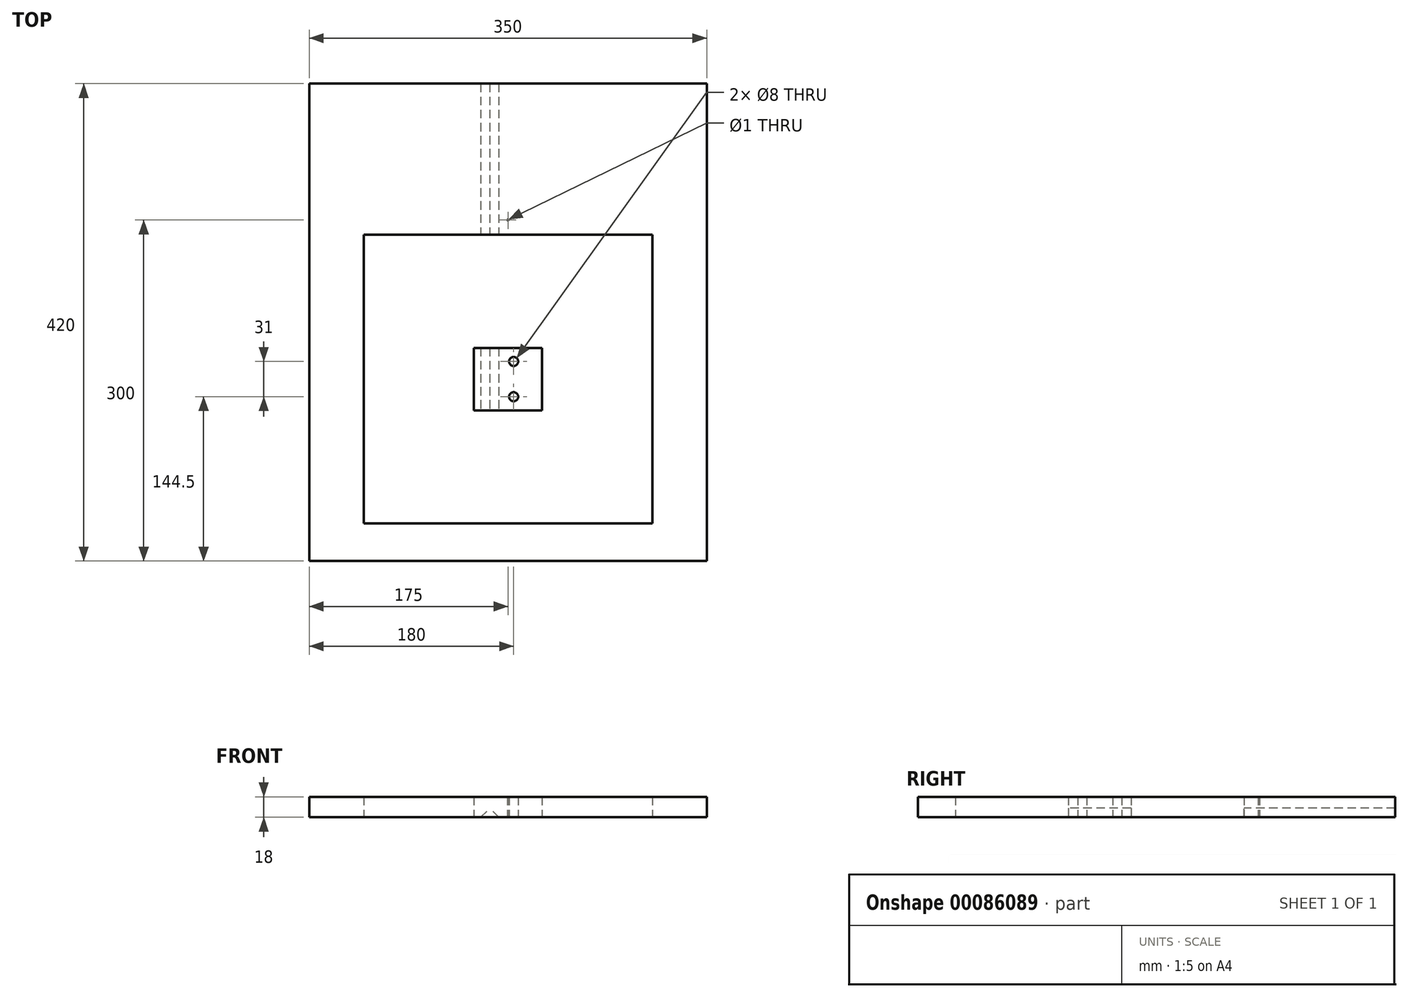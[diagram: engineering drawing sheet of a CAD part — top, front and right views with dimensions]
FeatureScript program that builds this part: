
annotation { "Feature Type Name" : "Feature", "Feature Type Description" : "" }
export const myFeature = defineFeature(function(context is Context, id is Id, definition is map)
    precondition{}
    {
        {
            var Q0;
            Q0=qCreatedBy(makeId("Top.planeOp"),FACE);
            var sketch = newSketch(context, id + "F0", { "sketchPlane" : qUnion([Q0])});
            skLineSegment(sketch, "E0.bottom", {"start": v(-175, 260) * mm, "end": v(175, 260) * mm});
            skLineSegment(sketch, "E0.top", {"start": v(-175, -160) * mm, "end": v(175, -160) * mm});
            skLineSegment(sketch, "E0.left", {"start": v(-175, 260) * mm, "end": v(-175, -160) * mm});
            skLineSegment(sketch, "E0.right", {"start": v(175, 260) * mm, "end": v(175, -160) * mm});
            skLineSegment(sketch, "E1.bottom", {"start": v(-107, 107) * mm, "end": v(107, 107) * mm, "construction": true});
            skLineSegment(sketch, "E1.top", {"start": v(-107, -107) * mm, "end": v(107, -107) * mm, "construction": true});
            skLineSegment(sketch, "E1.left", {"start": v(-107, 107) * mm, "end": v(-107, -107) * mm, "construction": true});
            skLineSegment(sketch, "E1.right", {"start": v(107, 107) * mm, "end": v(107, -107) * mm, "construction": true});
            skPoint(sketch, "E1.middle", {"position": v(0, 0) * mm});
            skLineSegment(sketch, "E2.bottom", {"start": v(-127, 127) * mm, "end": v(127, 127) * mm});
            skLineSegment(sketch, "E2.top", {"start": v(-127, -127) * mm, "end": v(127, -127) * mm});
            skLineSegment(sketch, "E2.left", {"start": v(-127, 127) * mm, "end": v(-127, -127) * mm});
            skLineSegment(sketch, "E2.right", {"start": v(127, 127) * mm, "end": v(127, -127) * mm});
            skPoint(sketch, "E3", {"position": v(0, 140) * mm});
            skPoint(sketch, "E3.positionSnap0", {"position": v(0, 260) * mm});
            skSolve(sketch);
        }
        {
            var Q0;
            Q0=makeQuery(id+"F0.imprint","IMPRINT",FACE,{"disambiguationData":[TD([[makeQuery(id+"F0.imprint","IMPRINT",EDGE,{"derivedFrom":sQuery(id+"F0.wireOp",EDGE,"E0.bottom")}),-1.0]])]});
            extrude(context, id + "F1", {"entities" : qUnion([Q0]), "depth" : 18 * mm});
        }
        {
            var Q0;
            Q0=sQuery(id+"F0.wireOp",VERTEX,"E3");
            var Q1;
            Q1=makeQuery(id+"F1.opExtrude","SWEPT_BODY",BODY,{"disambiguationData":[OSD([sQuery(id+"F0.wireOp",EDGE,"E0.bottom"),sQuery(id+"F0.wireOp",EDGE,"E0.top"),sQuery(id+"F0.wireOp",EDGE,"E0.left"),sQuery(id+"F0.wireOp",EDGE,"E0.right"),sQuery(id+"F0.wireOp",EDGE,"E2.bottom"),sQuery(id+"F0.wireOp",EDGE,"E2.top"),sQuery(id+"F0.wireOp",EDGE,"E2.left"),sQuery(id+"F0.wireOp",EDGE,"E2.right")])]});
            hole(context, id + "F2", {"style" : HoleStyle.SIMPLE, "endStyle" : HoleEndStyle.THROUGH, "oppositeDirection" : true, "holeDiameter" : 1 * mm, "locations" : qUnion([Q0]), "scope" : qUnion([Q1]), "isTappedThrough" : true});
        }
        {
            var Q0;
            Q0=qCreatedBy(makeId("Top.planeOp"),FACE);
            var sketch = newSketch(context, id + "F3", { "sketchPlane" : qUnion([Q0])});
            skLineSegment(sketch, "E4.bottom", {"start": v(30, 27.5) * mm, "end": v(-30, 27.5) * mm});
            skLineSegment(sketch, "E4.top", {"start": v(30, -27.5) * mm, "end": v(-30, -27.5) * mm});
            skLineSegment(sketch, "E4.left", {"start": v(30, 27.5) * mm, "end": v(30, -27.5) * mm});
            skLineSegment(sketch, "E4.right", {"start": v(-30, 27.5) * mm, "end": v(-30, -27.5) * mm});
            skPoint(sketch, "E4.middle", {"position": v(0, 0) * mm});
            skPoint(sketch, "E5", {"position": v(5, 15.5) * mm});
            skCircle(sketch, "E6", {"center": v(5, 15.5) * mm, "radius": 11 * mm, "construction": true});
            skPoint(sketch, "E7.MirrorP", {"position": v(5, -15.5) * mm});
            skCircle(sketch, "E8.MirrorC", {"center": v(5, -15.5) * mm, "radius": 11 * mm, "construction": true});
            skLineSegment(sketch, "E9.bottom", {"start": v(-24, 27.5) * mm, "end": v(-9, 27.5) * mm, "construction": true});
            skLineSegment(sketch, "E9.top", {"start": v(-24, -27.5) * mm, "end": v(-9, -27.5) * mm, "construction": true});
            skLineSegment(sketch, "E9.left", {"start": v(-24, 27.5) * mm, "end": v(-24, -27.5) * mm, "construction": true});
            skLineSegment(sketch, "E9.right", {"start": v(-9, 27.5) * mm, "end": v(-9, -27.5) * mm, "construction": true});
            skSolve(sketch);
        }
        {
            var Q0;
            Q0=makeQuery(id+"F3.imprint","IMPRINT",FACE,{"disambiguationData":[TD([[makeQuery(id+"F3.imprint","IMPRINT",EDGE,{"derivedFrom":sQuery(id+"F3.wireOp",EDGE,"E4.bottom")}),1.0]])]});
            extrude(context, id + "F4", {"entities" : qUnion([Q0]), "depth" : 18 * mm});
        }
        {
            var Q0;
            Q0=sQuery(id+"F3.wireOp",VERTEX,"E5");
            var Q1;
            Q1=sQuery(id+"F3.wireOp",VERTEX,"E7.MirrorP");
            var Q2;
            Q2=makeQuery(id+"F4.opExtrude","SWEPT_BODY",BODY,{"disambiguationData":[OSD([sQuery(id+"F3.wireOp",EDGE,"E4.bottom"),sQuery(id+"F3.wireOp",EDGE,"E4.top"),sQuery(id+"F3.wireOp",EDGE,"E4.left"),sQuery(id+"F3.wireOp",EDGE,"E4.right")])]});
            hole(context, id + "F5", {"style" : HoleStyle.SIMPLE, "endStyle" : HoleEndStyle.THROUGH, "oppositeDirection" : true, "holeDiameter" : 8 * mm, "locations" : qUnion([Q0, Q1]), "scope" : qUnion([Q2]), "isTappedThrough" : true});
        }
        {
            var Q0;
            Q0=makeQuery(id+"F4.opExtrude","SWEPT_FACE",FACE,{"disambiguationData":[OSD([sQuery(id+"F3.wireOp",EDGE,"E4.top")])]});
            var sketch = newSketch(context, id + "F6", { "sketchPlane" : qUnion([Q0])});
            skLineSegment(sketch, "E10", {"start": v(-16, 0) * mm, "end": v(-16, 18) * mm, "construction": true});
            skPoint(sketch, "E11", {"position": v(-16, 8) * mm});
            skLineSegment(sketch, "E12", {"start": v(-16, 8) * mm, "end": v(-8, 0) * mm});
            skLineSegment(sketch, "E13.MirrorCS", {"start": v(-16, 8) * mm, "end": v(-24, 0) * mm});
            skCircle(sketch, "E14", {"center": v(-16, -3) * mm, "radius": 7.5 * mm, "construction": true});
            skSolve(sketch);
        }
        {
            var Q0;
            Q0 = qSketchRegion(id + "F6", true);
            var Q1;
            {var subQ0=sQuery(id+"F6.wireOp",EDGE,"E12");Q1=makeQuery(id+"F6.imprint","IMPRINT",FACE,{"disambiguationData":[TD([[makeQuery(id+"F6.imprint","IMPRINT",EDGE,{"derivedFrom":subQ0}),-1.0]])]});}
            extrude(context, id + "F7", {"entities" : qUnion([Q0, Q1]), "operationType" : NewBodyOperationType.REMOVE, "endBound" : BoundingType.THROUGH_ALL, "oppositeDirection" : true, "depth" : 25 * mm});
        }
    });
